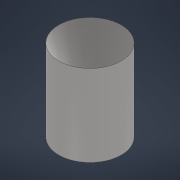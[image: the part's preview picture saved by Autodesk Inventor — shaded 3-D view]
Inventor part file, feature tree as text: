
AUTODESK INVENTOR PART (.ipt)
format: ipt  version: 2021 (Build 250183000, 183)  size: 92,672 bytes
history: native  units: mm
features: extrude x1, sketch x1
ambient origin geometry x8: Origin, YZ Plane, XZ Plane, XY Plane, X Axis, Y Axis, Z Axis, Center Point
bodies: Solid1 (feature_tree)
feature tree (2):
  extrude  "Extrusion1"  Depth=30.0mm TaperAngle=0.0deg
  sketch  "Sketch1"  dims[d0=23.0mm d1=30.0mm d2=0.0mm]
